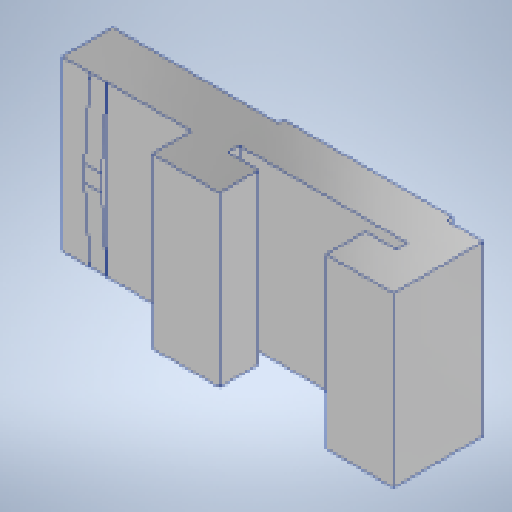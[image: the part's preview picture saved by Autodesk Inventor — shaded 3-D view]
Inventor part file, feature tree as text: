
AUTODESK INVENTOR PART (.ipt)
format: ipt  version: 2025 (Build 290162010, 162A)  size: 173,056 bytes
history: native  units: mm
features: reference x5, other x3, extrude x2, chamfer x2, sketch x2
ambient origin geometry x8: Origin, YZ Plane, XZ Plane, XY Plane, X Axis, Y Axis, Z Axis, Center Point
bodies: Volumenkörper1 (feature_tree)
feature tree (14):
  extrude  "Extrusion1"  Depth=7.0mm
  chamfer  "Fasen1"  Distance=16.0mm
  chamfer  "Fasen2"  Distance=12.0mm
  extrude  "Extrusion2"  Depth=2.0mm
  sketch  "Skizze1"  dims[d0=2.0mm d1=7.0mm]
  reference  "Referenz1"
  reference  "Referenz2"
  reference  "Referenz3"
  reference  "Referenz4"
  reference  "Referenz5"
  sketch  "Skizze2"  dims[d2=12.0mm d3=16.0mm d4=12.0mm d5=2.0mm d6=3.0mm d7=38.0mm d8=5.0mm d9=1.0mm d10=30.0mm d11=0.0mm d12=1.0mm d13=13.5mm d14=45.0deg d15=1.0mm d16=13.5mm d17=45.0deg d18=1.0mm d19=0.0mm d20=1.0mm d21=5.0mm]
  other  "<userpath>\GIT\HDVKBM\CAD\Krandemonstrator\FEM-Träger-Baugruppe6.iam"
  other  "FEM-Träger-Baugruppe6.iam"
  other  "TrägerUI:1"
